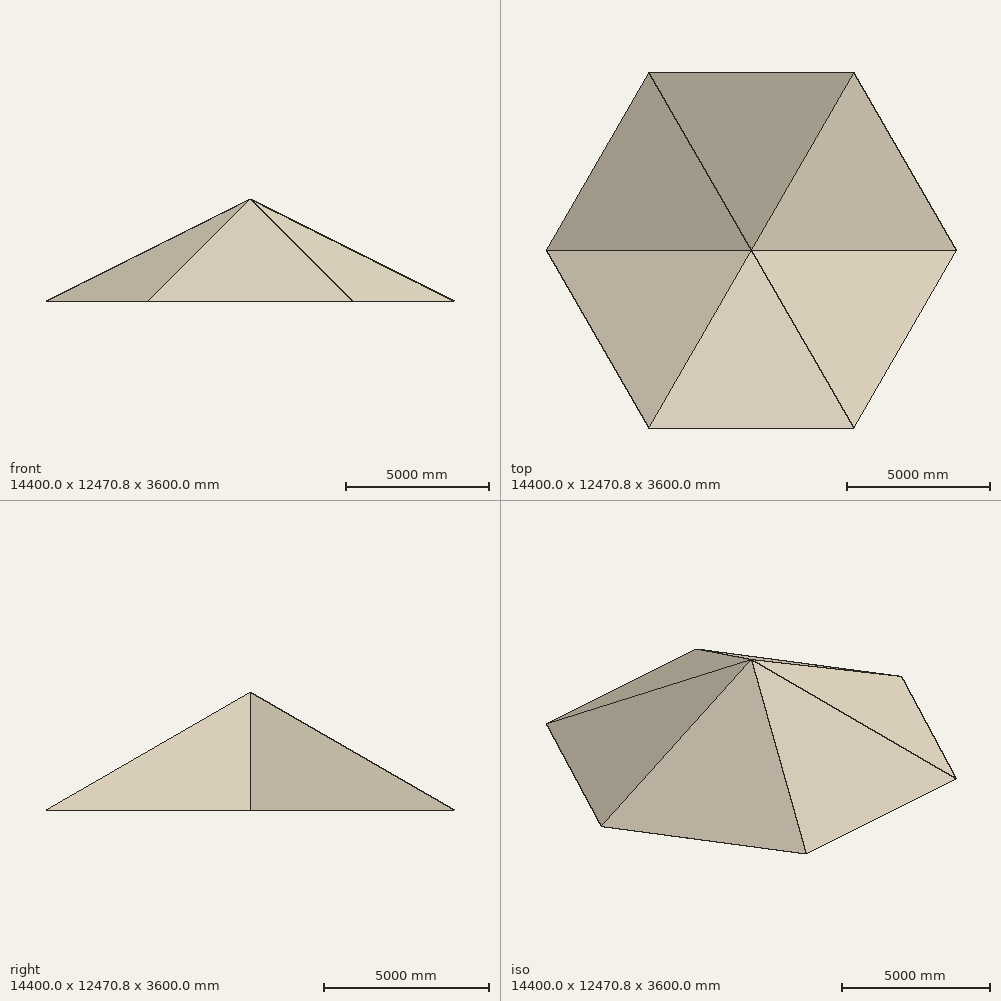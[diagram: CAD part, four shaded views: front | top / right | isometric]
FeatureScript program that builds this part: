
annotation { "Feature Type Name" : "Feature", "Feature Type Description" : "" }
export const myFeature = defineFeature(function(context is Context, id is Id, definition is map)
    precondition{}
    {
        {
            var Q0;
            Q0=qCreatedBy(makeId("Top.planeOp"),FACE);
            var sketch = newSketch(context, id + "F0", { "sketchPlane" : qUnion([Q0])});
            skCircle(sketch, "E0.cCircle", {"center": v(0, 0) * mm, "radius": 7200 * mm, "construction": true});
            skLineSegment(sketch, "E0.0", {"start": v(7200, 0) * mm, "end": v(3600, -6235.38) * mm});
            skLineSegment(sketch, "E0.1", {"start": v(3600, -6235.38) * mm, "end": v(-3600, -6235.38) * mm});
            skLineSegment(sketch, "E0.2", {"start": v(-3600, -6235.38) * mm, "end": v(-7200, 0) * mm});
            skLineSegment(sketch, "E0.3", {"start": v(-7200, 0) * mm, "end": v(-3600, 6235.38) * mm});
            skLineSegment(sketch, "E0.4", {"start": v(-3600, 6235.38) * mm, "end": v(3600, 6235.38) * mm});
            skLineSegment(sketch, "E0.5", {"start": v(3600, 6235.38) * mm, "end": v(7200, 0) * mm});
            skCircle(sketch, "E1.cCircle", {"center": v(0, 0) * mm, "radius": 7000 * mm, "construction": true});
            skLineSegment(sketch, "E1.0", {"start": v(7000, 0) * mm, "end": v(3500, -6062.18) * mm});
            skLineSegment(sketch, "E1.1", {"start": v(3500, -6062.18) * mm, "end": v(-3500, -6062.18) * mm});
            skLineSegment(sketch, "E1.2", {"start": v(-3500, -6062.18) * mm, "end": v(-7000, 0) * mm});
            skLineSegment(sketch, "E1.3", {"start": v(-7000, 0) * mm, "end": v(-3500, 6062.18) * mm});
            skLineSegment(sketch, "E1.4", {"start": v(-3500, 6062.18) * mm, "end": v(3500, 6062.18) * mm});
            skLineSegment(sketch, "E1.5", {"start": v(3500, 6062.18) * mm, "end": v(7000, 0) * mm});
            skSolve(sketch);
        }
        {
            var Q0;
            Q0 = qSketchRegion(id + "F0", true);
            var Q1;
            Q1=makeQuery(id+"F0.imprint","IMPRINT",FACE,{"disambiguationData":[TD([[makeQuery(id+"F0.imprint","IMPRINT",EDGE,{"derivedFrom":sQuery(id+"F0.wireOp",EDGE,"E1.0")}),-1.0]])]});
            extrude(context, id + "F1", {"entities" : qUnion([Q0, Q1]), "depth" : 3600 * mm, "offsetDistance" : 25 * mm});
        }
        {
            var Q0;
            Q0=makeQuery(id+"F1.opExtrude","CAP_EDGE",EDGE,{"disambiguationData":[OSD([sQuery(id+"F0.wireOp",EDGE,"E0.2")])],"isStart":false});
            var Q1;
            Q1=makeQuery(id+"F1.opExtrude","CAP_EDGE",EDGE,{"disambiguationData":[OSD([sQuery(id+"F0.wireOp",EDGE,"E0.3")])],"isStart":false});
            var Q2;
            Q2=makeQuery(id+"F1.opExtrude","CAP_EDGE",EDGE,{"disambiguationData":[OSD([sQuery(id+"F0.wireOp",EDGE,"E0.4")])],"isStart":false});
            var Q3;
            Q3=makeQuery(id+"F1.opExtrude","CAP_EDGE",EDGE,{"disambiguationData":[OSD([sQuery(id+"F0.wireOp",EDGE,"E0.5")])],"isStart":false});
            var Q4;
            Q4=makeQuery(id+"F1.opExtrude","CAP_EDGE",EDGE,{"disambiguationData":[OSD([sQuery(id+"F0.wireOp",EDGE,"E0.0")])],"isStart":false});
            var Q5;
            Q5=makeQuery(id+"F1.opExtrude","CAP_EDGE",EDGE,{"disambiguationData":[OSD([sQuery(id+"F0.wireOp",EDGE,"E0.1")])],"isStart":false});
            chamfer(context, id + "F2", {"entities" : qUnion([Q0, Q1, Q2, Q3, Q4, Q5]), "chamferType" : ChamferType.OFFSET_ANGLE, "width" : 3600 * mm, "oppositeDirection" : false, "angle" : 60 * degree, "tangentPropagation" : true});
        }
        {
            var Q0;
            Q0=makeQuery(id+"F1.opExtrude","CAP_FACE",FACE,{"disambiguationData":[OSD([sQuery(id+"F0.wireOp",EDGE,"E0.0"),sQuery(id+"F0.wireOp",EDGE,"E0.1"),sQuery(id+"F0.wireOp",EDGE,"E0.2"),sQuery(id+"F0.wireOp",EDGE,"E0.3"),sQuery(id+"F0.wireOp",EDGE,"E0.4"),sQuery(id+"F0.wireOp",EDGE,"E0.5")])],"isStart":true});
            shell(context, id + "F3", {"entities" : qUnion([Q0]), "thickness" : 200 * mm});
        }
    });
